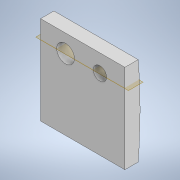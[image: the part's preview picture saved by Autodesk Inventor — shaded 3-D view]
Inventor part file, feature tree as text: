
AUTODESK INVENTOR PART (.ipt)
format: ipt  version: 2021.1 (Build 251245000, 245)  size: 123,392 bytes
history: native  units: in
note: dims shown in document units (in); Inventor stores cm internally (conversion verified against a paired STEP export)
features: extrude x2, sketch x2, plane x1, split x1
ambient origin geometry x8: Origin, YZ Plane, XZ Plane, XY Plane, X Axis, Y Axis, Z Axis, Center Point
bodies: Solid1 (feature_tree)
feature tree (6):
  extrude  "Extrusion1"  Depth=4.0in
  extrude  "Extrusion2"  Depth=24.0in
  plane  "Work Plane1"
  split  "Split1"
  sketch  "Sketch1"  dims[d0=0.6in d1=4.0in]
  sketch  "Sketch2"  dims[d3=2.0in d4=0.0835in d5=24.0in d6=4.0in d7=24.0in d9=3.8in d10=0.0in d11=0.8in d12=0.6in d13=2.25in d14=0.775in d18=0.0in d19=0.0in d20=0.8in d21=-0.8in]
